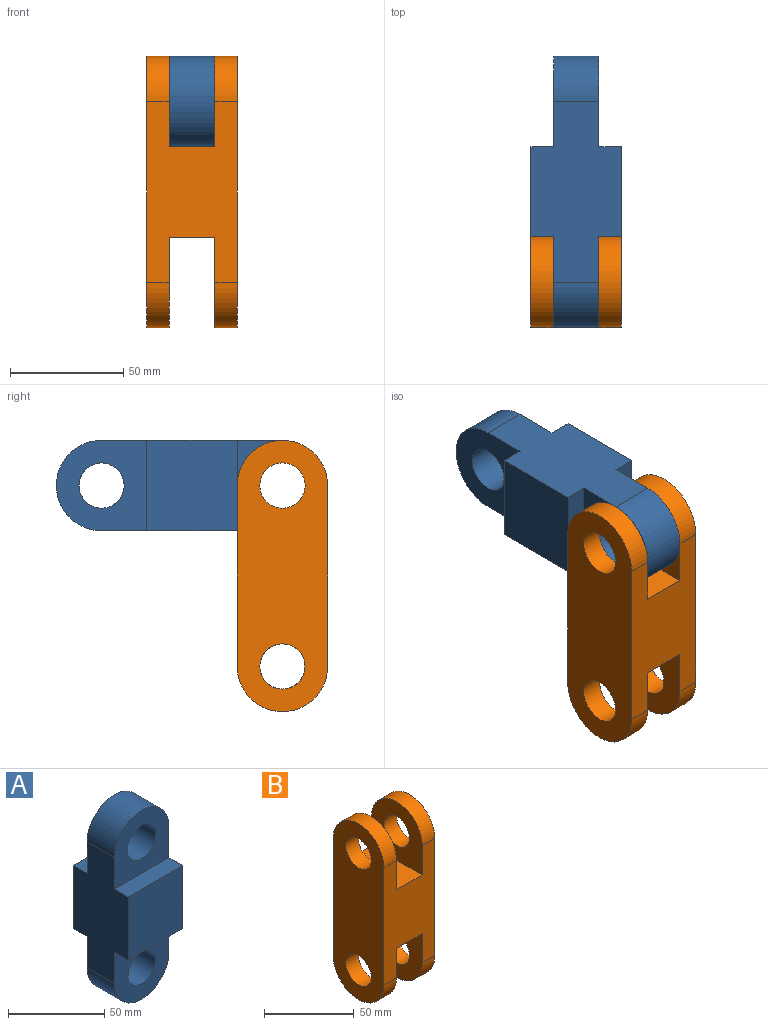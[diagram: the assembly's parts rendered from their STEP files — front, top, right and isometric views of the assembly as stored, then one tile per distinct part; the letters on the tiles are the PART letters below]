
ASSEMBLY  parts=2 mates=3
PART A: 16 faces, bbox 40x40x120 mm
  f0: plane 40x40mm, normal (0,-1,0), area 1114.2mm2, adj f1,f2,f5,f13,f15
  f1: plane 80x40mm, normal (1,0,0), area 2400mm2, adj f0,f3,f4,f5,f6,f7,f8,f9
  f2: plane 80x40mm, normal (-1,0,0), area 2400mm2, adj f0,f3,f4,f5,f6,f7,f8,f9
  f3: plane 40x40mm, normal (0,-1,0), area 1079.5mm2, adj f1,f2,f4,f12,f14
  f4: plane 40x10mm, normal (0,0,1), area 400mm2, adj f1,f2,f3,f6
  f5: plane 40x10mm, normal (0,0,-1), area 400mm2, adj f0,f1,f2,f6
  f6: plane 40x40mm, normal (0,-1,0), area 1600mm2, adj f1,f2,f4,f5
  f7: plane 40x40mm, normal (0,1,0), area 1114.2mm2, adj f1,f2,f10,f13,f15
  f8: plane 40x40mm, normal (0,1,0), area 1079.5mm2, adj f1,f2,f9,f12,f14
  f9: plane 40x10mm, normal (0,0,1), area 400mm2, adj f1,f2,f8,f11
  f10: plane 40x10mm, normal (0,0,-1), area 400mm2, adj f1,f2,f7,f11
  f11: plane 40x40mm, normal (0,1,0), area 1600mm2, adj f1,f2,f9,f10
  f12: cylinder r=10.54mm len=21.07mm, axis (0,-1,0), area 1324.1mm2, adj f3,f8
  f13: cylinder r=10mm len=20mm, axis (0,1,0), area 1256.6mm2, adj f0,f7
  f14: cylinder r=20mm len=40mm, axis (0,-1,0), area 1256.6mm2, adj f1,f2,f3,f8
  f15: cylinder r=20mm len=40mm, axis (0,-1,0), area 1256.6mm2, adj f0,f1,f2,f7
PART B: 18 faces, bbox 40.2x40x120 mm
  f0: plane 40x20.2mm, normal (0,0,1), area 808mm2, adj f1,f2,f6,f10
  f1: plane 80x40.2mm, normal (0,1,0), area 2408mm2, adj f0,f3,f4,f6,f7,f8,f10,f11
  f2: plane 80x40.2mm, normal (0,-1,0), area 2408mm2, adj f0,f3,f4,f6,f7,f8,f10,f11
  f3: plane 120x40mm, normal (1,0,0), area 3828.3mm2, adj f1,f2,f4,f5,f15,f17
  f4: cylinder r=20mm len=40mm, axis (1,0,0), area 628.3mm2, adj f1,f2,f3,f6
  f5: cylinder r=10mm len=20mm, axis (1,0,0), area 628.3mm2, adj f3,f6
  f6: plane 40x40mm, normal (-1,0,0), area 1114.2mm2, adj f0,f1,f2,f4,f5
  f7: plane 120x40mm, normal (-1,0,0), area 3828.3mm2, adj f1,f2,f8,f9,f14,f16
  f8: cylinder r=20mm len=40mm, axis (-1,0,0), area 628.3mm2, adj f1,f2,f7,f10
  f9: cylinder r=10mm len=20mm, axis (-1,0,0), area 628.3mm2, adj f7,f10
  f10: plane 40x40mm, normal (1,0,0), area 1114.2mm2, adj f0,f1,f2,f8,f9
  f11: plane 40x40mm, normal (-1,0,0), area 1114.2mm2, adj f1,f2,f12,f15,f17
  f12: plane 40x20.2mm, normal (0,0,-1), area 808mm2, adj f1,f2,f11,f13
  f13: plane 40x40mm, normal (1,0,0), area 1114.2mm2, adj f1,f2,f12,f14,f16
  f14: cylinder r=10mm len=20mm, axis (1,0,0), area 628.3mm2, adj f7,f13
  f15: cylinder r=10mm len=20mm, axis (1,0,0), area 628.3mm2, adj f3,f11
  f16: cylinder r=20mm len=40mm, axis (-1,0,0), area 628.3mm2, adj f1,f2,f7,f13
  f17: cylinder r=20mm len=40mm, axis (1,0,0), area 628.3mm2, adj f1,f2,f3,f11
PLACE A rot(axis=(0.58,-0.58,0.58),120deg) t=(28.62,53.66,57.2)mm
PLACE B t=(28.52,13.66,-2.8)mm
MATE planar B.f4 <-> A.f12  axis (-1,0,0) through (8.42,13.66,57.2)mm
MATE planar A.f14 <-> B.f4  axis (1,0,0) through (38.62,13.66,57.2)mm
MATE parallel A.f12 <-> B.f4  axis (1,0,0) through (38.62,13.66,57.2)mm
